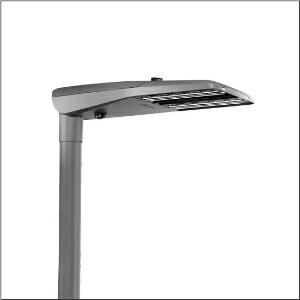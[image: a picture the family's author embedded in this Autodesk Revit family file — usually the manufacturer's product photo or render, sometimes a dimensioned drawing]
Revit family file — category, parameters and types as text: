
# Revit family: streetlight_sl_11_iq_midi___pc-l_5xc3e21y08me_ec69
name_source: partatom
category: Lighting Fixtures
units: mm (PartAtom-declared; Revit-internal decimal feet)

## family parameters
Cut with Voids When Loaded = No
Host = Face
Light Source = No
Part Type = Normal
Room Calculation Point = No
Round Connector Dimension = Use Diameter
Shared = No

## types (1)
- --- (1 x LED, 12730 lm, 122.8 W, 2200K)
    Apparent Load = 123 VA
    CIE Flux Codes = 37 73 96 100 100
    Color Rendering = 70
    Color Temperature = 2200K
    Default Elevation = 1800 mm
    Description = Streetlight SL 11 iQ midi, mast luminaire, primary light control with 3 zone facetted reflector, of plastic, silver coated, highly specular, primary optical cover: cover, of PMMA, transparent, light distribution: PC-L, light emission: direct distribution, primary light characteristic: asymmetric, left, installation type: post-top, side-entry, LED, High Power LED, rated luminous flux: 12.730lm, luminous efficacy: 104lm/W, light colour: 722, colour temperature: 2200K, control: presetting dimming logarithmic, Street-Remote, Auto-Match, Temp-Guard, Lumen-Switch, Night-Set, Smart-Wire, Light-Fading, Desk-Remote (wireless, voltage-free reading and setting of iQ features in the workshop via application-optimized NFC function/RFID function), optimised constant luminous flux control (CLO 2.0), with cable H07RN-F 5x 1.5mm², mains connection: 230..240V, AC, 50/60Hz, connection cable pre-assembled, cable length: 12,5m, start of lifetime: 123W, end of service life: 130W, reduction: 56W, luminaire housing, of diecast aluminium, powder-coated, Siteco® metallic grey (DB 702S), please order mast flange separately, inclination adjustable without tools: 0°, 5°, 10°, 15° (post-top) | 0°, -5°, -10°, -15° (side-entry), sealing non-destructively replaceable, multi-level sealing system, length: 780mm, width: 376mm, height: 118mm, mast flange for spigot size: 42mm (side-entry): 5XC10008XM4, 60/48mm (side-entry/post-top): 5XC10108XM2, 76/60mm (side-entry/post-top): 5XC10108XM1, equipment: Power, Smart Interface below and above, protection rating (complete): IP66, insulation class (complete): insulation class II (safety insulation), certification: CE, ENEC, VDE, UKCA, impact resistance: IK09, permissible operating ambient temperature for outdoor applications: -25..+50°C, standard-compliant lighting for roads and squares, Environmental Product Declaration (EPD) tested and certified by an independent institute, packaging unit: 1 piece

Light Distribution: PC-L
    Height = 118 mm
    Lamp = 1 x LED
    Lamp Light Flux = 12730 lm
    Lamp Power = 122.8 W
    Lamp count = 1
    Length = 780 mm
    Luminous efficacy = 104 lm/W
    Manufacturer = Siteco
    ModVariant = No
    Model = 5XC3E21Y08ME
    Number of Poles = 1
    OnlyDefault = Yes
    Power Factor = 1
    Product Name = Streetlight SL 11 iQ midi | PC-L
    Product group = mast luminaire | pylon top
    ProductGroupID = 6100
    Protection Class = Protection class II
    Protection Degree = IP 66
    RLX_Detail_Level = 1
    RLX_Emergency_Light_Flux = 0 lm
    RLX_Emergency_Type = 0
    RLX_Emergency_Type_DB = No
    RlxData = <blob elided: 73493 chars, md5=7b540fdb>
    Socket = socket
    Standby Power = 0 W
    System Light Flux = 12729 lm
    System Power = 123 W
    Type Comments = factory setting: luminous flux: 100 % | dim-lin: 254 | 553 mA
    Type Image = l_1004429.jpg
    URL = http://relux.com
    VarID = @adj_058299
    Voltage = 0 V
    Weight = 0.00 kg
    Width = 376 mm

## geometry (parser evidence)
native form markers: Blend x4, Sweep x10
no freeform markers — native parametric forms only
